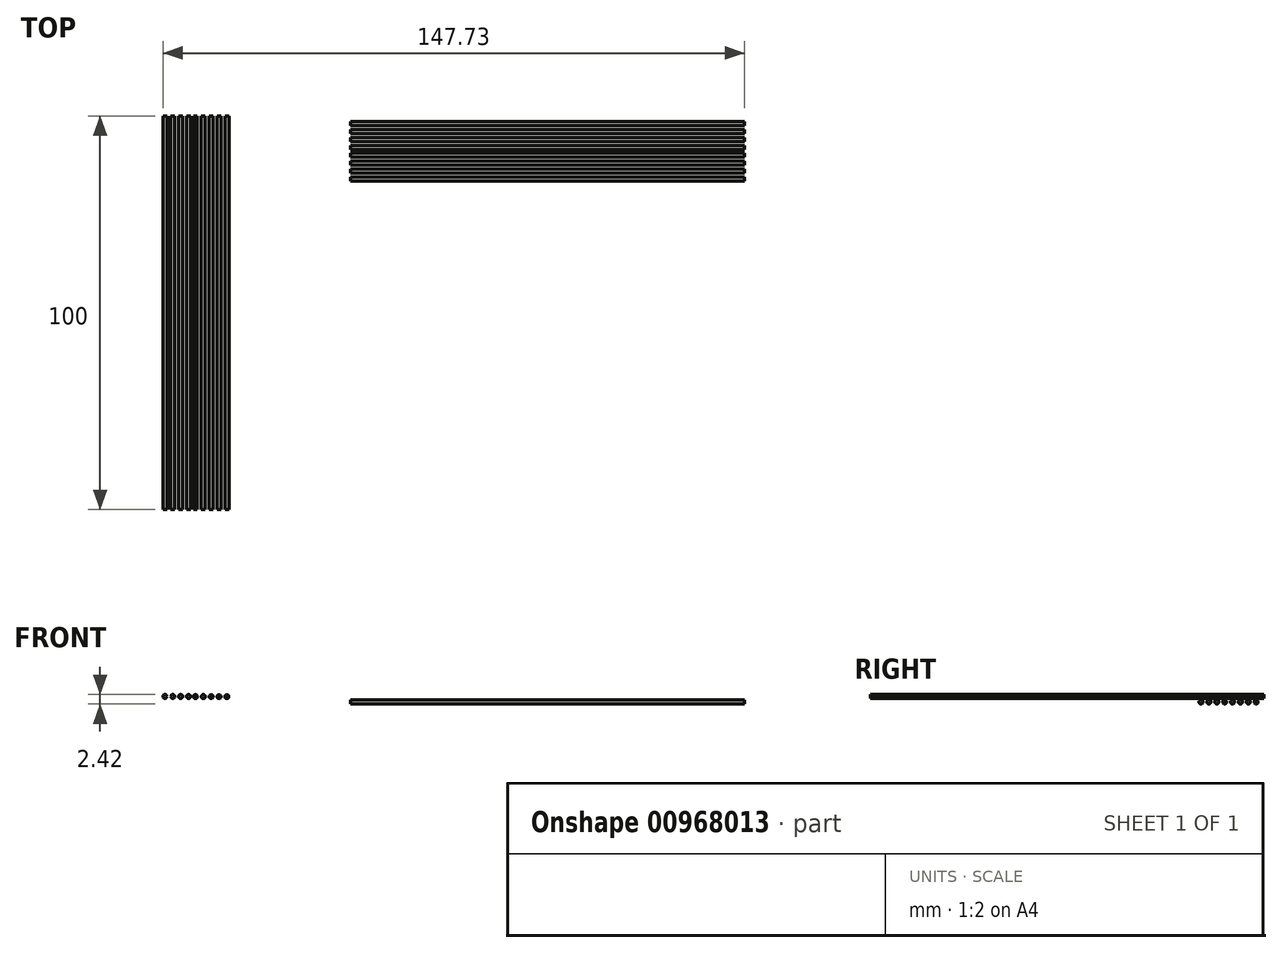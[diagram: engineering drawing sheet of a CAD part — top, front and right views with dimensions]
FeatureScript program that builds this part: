
annotation { "Feature Type Name" : "Feature", "Feature Type Description" : "" }
export const myFeature = defineFeature(function(context is Context, id is Id, definition is map)
    precondition{}
    {
        {
            var Q0;
            Q0=qCreatedBy(makeId("Front.planeOp"),FACE);
            var sketch = newSketch(context, id + "F0", { "sketchPlane" : qUnion([Q0])});
            skLineSegment(sketch, "E0", {"start": v(0, 0) * mm, "end": v(48.45, 0.2) * mm});
            skLineSegment(sketch, "E1", {"start": v(0, 0) * mm, "end": v(-47.23, 0.2) * mm});
            skCircle(sketch, "E2", {"center": v(-47.23, 0.2) * mm, "radius": 0.5 * mm});
            skCircle(sketch, "E3", {"center": v(-45.23, 0.2) * mm, "radius": 0.5 * mm});
            skCircle(sketch, "E4", {"center": v(-43.23, 0.19) * mm, "radius": 0.5 * mm});
            skCircle(sketch, "E5", {"center": v(-41.23, 0.18) * mm, "radius": 0.5 * mm});
            skCircle(sketch, "E6", {"center": v(-39.5, 0.17) * mm, "radius": 0.5 * mm});
            skSolve(sketch);
        }
        {
            var Q0;
            Q0=qCreatedBy(makeId("Front.planeOp"),FACE);
            var sketch = newSketch(context, id + "F1", { "sketchPlane" : qUnion([Q0])});
            skCircle(sketch, "E7", {"center": v(-37.5, 0.16) * mm, "radius": 0.5 * mm});
            skCircle(sketch, "E8", {"center": v(-35.5, 0.15) * mm, "radius": 0.5 * mm});
            skCircle(sketch, "E9", {"center": v(0, 0) * mm, "radius": 0.5 * mm});
            skCircle(sketch, "E10", {"center": v(-33.5, 0.14) * mm, "radius": 0.5 * mm});
            skCircle(sketch, "E11", {"center": v(-31.5, 0.14) * mm, "radius": 0.5 * mm});
            skSolve(sketch);
        }
        {
            var Q0;
            Q0=makeQuery(id+"F0.imprint","IMPRINT",FACE,{"disambiguationData":[TD([[makeQuery(id+"F0.imprint","IMPRINT",EDGE,{"derivedFrom":sQuery(id+"F0.wireOp",EDGE,"E2")}),1.0]])]});
            var Q1;
            {var subQ0=sQuery(id+"F0.wireOp",EDGE,"E3");var subQ1=sQuery(id+"F0.wireOp",EDGE,"E1");var subQ2=makeQuery(id+"F0.imprint","INTERSECT",VERTEX,{"disambiguationData":[OD(0.0)],"derivedFrom":[subQ1,subQ0]});Q1=makeQuery(id+"F0.imprint","IMPRINT",FACE,{"disambiguationData":[TD([[makeQuery(id+"F0.imprint","IMPRINT",EDGE,{"disambiguationData":[TD([[subQ2,1.0]])],"derivedFrom":subQ1}),-1.0]])]});}
            var Q2;
            {var subQ0=sQuery(id+"F0.wireOp",EDGE,"E3");var subQ1=sQuery(id+"F0.wireOp",EDGE,"E1");var subQ2=makeQuery(id+"F0.imprint","INTERSECT",VERTEX,{"disambiguationData":[OD(0.0)],"derivedFrom":[subQ1,subQ0]});Q2=makeQuery(id+"F0.imprint","IMPRINT",FACE,{"disambiguationData":[TD([[makeQuery(id+"F0.imprint","IMPRINT",EDGE,{"disambiguationData":[TD([[subQ2,1.0]])],"derivedFrom":subQ1}),1.0]])]});}
            var Q3;
            {var subQ0=sQuery(id+"F0.wireOp",EDGE,"E4");var subQ1=sQuery(id+"F0.wireOp",EDGE,"E1");var subQ2=makeQuery(id+"F0.imprint","INTERSECT",VERTEX,{"disambiguationData":[OD(0.0)],"derivedFrom":[subQ1,subQ0]});Q3=makeQuery(id+"F0.imprint","IMPRINT",FACE,{"disambiguationData":[TD([[makeQuery(id+"F0.imprint","IMPRINT",EDGE,{"disambiguationData":[TD([[subQ2,1.0]])],"derivedFrom":subQ1}),1.0]])]});}
            var Q4;
            {var subQ0=sQuery(id+"F0.wireOp",EDGE,"E4");var subQ1=sQuery(id+"F0.wireOp",EDGE,"E1");var subQ2=makeQuery(id+"F0.imprint","INTERSECT",VERTEX,{"disambiguationData":[OD(0.0)],"derivedFrom":[subQ1,subQ0]});Q4=makeQuery(id+"F0.imprint","IMPRINT",FACE,{"disambiguationData":[TD([[makeQuery(id+"F0.imprint","IMPRINT",EDGE,{"disambiguationData":[TD([[subQ2,1.0]])],"derivedFrom":subQ1}),-1.0]])]});}
            var Q5;
            {var subQ0=sQuery(id+"F0.wireOp",EDGE,"E5");var subQ1=sQuery(id+"F0.wireOp",EDGE,"E1");var subQ2=makeQuery(id+"F0.imprint","INTERSECT",VERTEX,{"disambiguationData":[OD(0.0)],"derivedFrom":[subQ1,subQ0]});Q5=makeQuery(id+"F0.imprint","IMPRINT",FACE,{"disambiguationData":[TD([[makeQuery(id+"F0.imprint","IMPRINT",EDGE,{"disambiguationData":[TD([[subQ2,1.0]])],"derivedFrom":subQ1}),-1.0]])]});}
            var Q6;
            {var subQ0=sQuery(id+"F0.wireOp",EDGE,"E5");var subQ1=sQuery(id+"F0.wireOp",EDGE,"E1");var subQ2=makeQuery(id+"F0.imprint","INTERSECT",VERTEX,{"disambiguationData":[OD(0.0)],"derivedFrom":[subQ1,subQ0]});Q6=makeQuery(id+"F0.imprint","IMPRINT",FACE,{"disambiguationData":[TD([[makeQuery(id+"F0.imprint","IMPRINT",EDGE,{"disambiguationData":[TD([[subQ2,1.0]])],"derivedFrom":subQ1}),1.0]])]});}
            var Q7;
            {var subQ0=sQuery(id+"F0.wireOp",EDGE,"E6");var subQ1=sQuery(id+"F0.wireOp",EDGE,"E1");var subQ2=makeQuery(id+"F0.imprint","INTERSECT",VERTEX,{"disambiguationData":[OD(0.0)],"derivedFrom":[subQ1,subQ0]});Q7=makeQuery(id+"F0.imprint","IMPRINT",FACE,{"disambiguationData":[TD([[makeQuery(id+"F0.imprint","IMPRINT",EDGE,{"disambiguationData":[TD([[subQ2,1.0]])],"derivedFrom":subQ1}),-1.0]])]});}
            var Q8;
            {var subQ0=sQuery(id+"F0.wireOp",EDGE,"E6");var subQ1=sQuery(id+"F0.wireOp",EDGE,"E1");var subQ2=makeQuery(id+"F0.imprint","INTERSECT",VERTEX,{"disambiguationData":[OD(0.0)],"derivedFrom":[subQ1,subQ0]});Q8=makeQuery(id+"F0.imprint","IMPRINT",FACE,{"disambiguationData":[TD([[makeQuery(id+"F0.imprint","IMPRINT",EDGE,{"disambiguationData":[TD([[subQ2,1.0]])],"derivedFrom":subQ1}),1.0]])]});}
            var Q9;
            Q9=makeQuery(id+"F1.imprint","IMPRINT",FACE,{"disambiguationData":[TD([[makeQuery(id+"F1.imprint","IMPRINT",EDGE,{"derivedFrom":sQuery(id+"F1.wireOp",EDGE,"E8")}),1.0]])]});
            var Q10;
            Q10=makeQuery(id+"F1.imprint","IMPRINT",FACE,{"disambiguationData":[TD([[makeQuery(id+"F1.imprint","IMPRINT",EDGE,{"derivedFrom":sQuery(id+"F1.wireOp",EDGE,"E10")}),1.0]])]});
            var Q11;
            Q11=makeQuery(id+"F1.imprint","IMPRINT",FACE,{"disambiguationData":[TD([[makeQuery(id+"F1.imprint","IMPRINT",EDGE,{"derivedFrom":sQuery(id+"F1.wireOp",EDGE,"E7")}),1.0]])]});
            var Q12;
            Q12=makeQuery(id+"F1.imprint","IMPRINT",FACE,{"disambiguationData":[TD([[makeQuery(id+"F1.imprint","IMPRINT",EDGE,{"derivedFrom":sQuery(id+"F1.wireOp",EDGE,"E11")}),1.0]])]});
            extrude(context, id + "F2", {"entities" : qUnion([Q0, Q1, Q2, Q3, Q4, Q5, Q6, Q7, Q8, Q9, Q10, Q11, Q12]), "depth" : 100 * mm, "offsetDistance" : 25 * mm});
        }
        {
            var Q0;
            Q0=qCreatedBy(makeId("Right.planeOp"),FACE);
            var sketch = newSketch(context, id + "F3", { "sketchPlane" : qUnion([Q0])});
            skCircle(sketch, "E12", {"center": v(-2, -1.22) * mm, "radius": 0.5 * mm});
            skCircle(sketch, "E13", {"center": v(-4, -1.22) * mm, "radius": 0.5 * mm});
            skCircle(sketch, "E14", {"center": v(-6, -1.22) * mm, "radius": 0.5 * mm});
            skCircle(sketch, "E15", {"center": v(-8, -1.22) * mm, "radius": 0.5 * mm});
            skCircle(sketch, "E16", {"center": v(-10, -1.22) * mm, "radius": 0.5 * mm});
            skCircle(sketch, "E17", {"center": v(-12, -1.22) * mm, "radius": 0.5 * mm});
            skCircle(sketch, "E18", {"center": v(-14, -1.22) * mm, "radius": 0.5 * mm});
            skCircle(sketch, "E19", {"center": v(-16, -1.22) * mm, "radius": 0.5 * mm});
            skLineSegment(sketch, "E20", {"start": v(0.92, 1.78) * mm, "end": v(-0.55, 1.78) * mm});
            skSolve(sketch);
        }
        {
            var Q0;
            Q0=makeQuery(id+"F3.imprint","IMPRINT",FACE,{"disambiguationData":[TD([[makeQuery(id+"F3.imprint","IMPRINT",EDGE,{"derivedFrom":sQuery(id+"F3.wireOp",EDGE,"E19")}),1.0]])]});
            var Q1;
            Q1=makeQuery(id+"F3.imprint","IMPRINT",FACE,{"disambiguationData":[TD([[makeQuery(id+"F3.imprint","IMPRINT",EDGE,{"derivedFrom":sQuery(id+"F3.wireOp",EDGE,"E18")}),1.0]])]});
            var Q2;
            Q2=makeQuery(id+"F3.imprint","IMPRINT",FACE,{"disambiguationData":[TD([[makeQuery(id+"F3.imprint","IMPRINT",EDGE,{"derivedFrom":sQuery(id+"F3.wireOp",EDGE,"E17")}),1.0]])]});
            var Q3;
            Q3=makeQuery(id+"F3.imprint","IMPRINT",FACE,{"disambiguationData":[TD([[makeQuery(id+"F3.imprint","IMPRINT",EDGE,{"derivedFrom":sQuery(id+"F3.wireOp",EDGE,"E16")}),1.0]])]});
            var Q4;
            Q4=makeQuery(id+"F3.imprint","IMPRINT",FACE,{"disambiguationData":[TD([[makeQuery(id+"F3.imprint","IMPRINT",EDGE,{"derivedFrom":sQuery(id+"F3.wireOp",EDGE,"E15")}),1.0]])]});
            var Q5;
            Q5=makeQuery(id+"F3.imprint","IMPRINT",FACE,{"disambiguationData":[TD([[makeQuery(id+"F3.imprint","IMPRINT",EDGE,{"derivedFrom":sQuery(id+"F3.wireOp",EDGE,"E14")}),1.0]])]});
            var Q6;
            Q6=makeQuery(id+"F3.imprint","IMPRINT",FACE,{"disambiguationData":[TD([[makeQuery(id+"F3.imprint","IMPRINT",EDGE,{"derivedFrom":sQuery(id+"F3.wireOp",EDGE,"E13")}),1.0]])]});
            var Q7;
            Q7=makeQuery(id+"F3.imprint","IMPRINT",FACE,{"disambiguationData":[TD([[makeQuery(id+"F3.imprint","IMPRINT",EDGE,{"derivedFrom":sQuery(id+"F3.wireOp",EDGE,"E12")}),1.0]])]});
            extrude(context, id + "F4", {"entities" : qUnion([Q0, Q1, Q2, Q3, Q4, Q5, Q6, Q7]), "depth" : 100 * mm, "offsetDistance" : 25 * mm});
        }
    });
